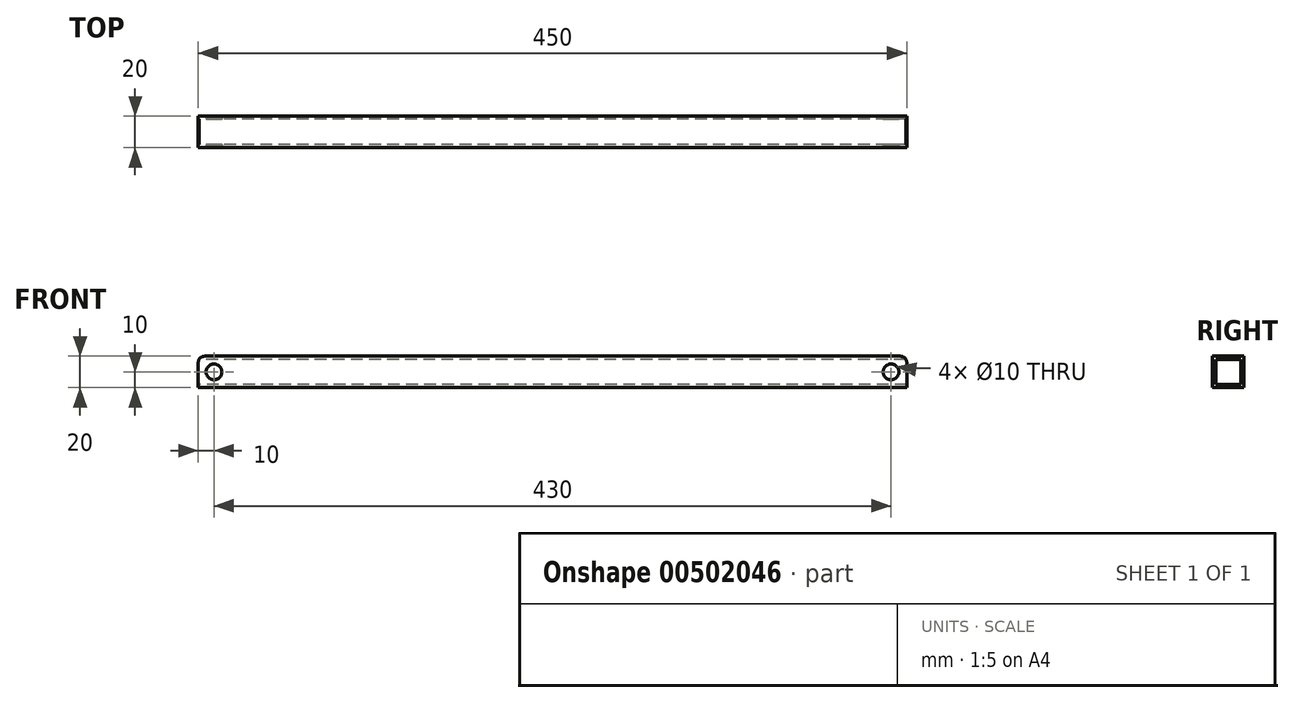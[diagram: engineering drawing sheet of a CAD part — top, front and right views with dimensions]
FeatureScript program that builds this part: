
annotation { "Feature Type Name" : "Feature", "Feature Type Description" : "" }
export const myFeature = defineFeature(function(context is Context, id is Id, definition is map)
    precondition{}
    {
        {
            var Q0;
            Q0=qCreatedBy(makeId("Right.planeOp"),FACE);
            var sketch = newSketch(context, id + "F0", { "sketchPlane" : qUnion([Q0])});
            skLineSegment(sketch, "E0.bottom", {"start": v(0, 0) * mm, "end": v(20, 0) * mm});
            skLineSegment(sketch, "E0.top", {"start": v(0, 20) * mm, "end": v(20, 20) * mm});
            skLineSegment(sketch, "E0.left", {"start": v(0, 0) * mm, "end": v(0, 20) * mm});
            skLineSegment(sketch, "E0.right", {"start": v(20, 0) * mm, "end": v(20, 20) * mm});
            skLineSegment(sketch, "E1.0", {"start": v(2, 18) * mm, "end": v(18, 18) * mm});
            skLineSegment(sketch, "E1.1", {"start": v(2, 2) * mm, "end": v(2, 18) * mm});
            skLineSegment(sketch, "E1.2", {"start": v(2, 2) * mm, "end": v(18, 2) * mm});
            skLineSegment(sketch, "E1.3", {"start": v(18, 2) * mm, "end": v(18, 18) * mm});
            skSolve(sketch);
        }
        {
            var Q0;
            Q0 = qSketchRegion(id + "F0", true);
            extrude(context, id + "F1", {"entities" : qUnion([Q0]), "depth" : 450 * mm});
        }
        {
            var Q0;
            Q0=makeQuery(id+"F1.opExtrude","SWEPT_FACE",FACE,{"disambiguationData":[OSD([sQuery(id+"F0.wireOp",EDGE,"E0.left")])]});
            var sketch = newSketch(context, id + "F2", { "sketchPlane" : qUnion([Q0])});
            skCircle(sketch, "E2", {"center": v(440, 10) * mm, "radius": 5 * mm});
            skSolve(sketch);
        }
        {
            var Q0;
            Q0 = qSketchRegion(id + "F2", true);
            extrude(context, id + "F3", {"entities" : qUnion([Q0]), "operationType" : NewBodyOperationType.REMOVE, "endBound" : BoundingType.THROUGH_ALL, "oppositeDirection" : true, "depth" : 25 * mm});
        }
        {
            var Q0;
            Q0=makeQuery(id+"F1.opExtrude","SWEPT_FACE",FACE,{"disambiguationData":[OSD([sQuery(id+"F0.wireOp",EDGE,"E0.left")])]});
            var sketch = newSketch(context, id + "F4", { "sketchPlane" : qUnion([Q0])});
            skCircle(sketch, "E3", {"center": v(10, 10) * mm, "radius": 5 * mm});
            skSolve(sketch);
        }
        {
            var Q0;
            Q0 = qSketchRegion(id + "F4", true);
            extrude(context, id + "F5", {"entities" : qUnion([Q0]), "operationType" : NewBodyOperationType.REMOVE, "endBound" : BoundingType.THROUGH_ALL, "oppositeDirection" : true, "depth" : 25 * mm});
        }
        {
            var Q0;
            Q0=makeQuery(id+"F1.opExtrude","CAP_EDGE",EDGE,{"disambiguationData":[OSD([sQuery(id+"F0.wireOp",EDGE,"E0.top")])],"isStart":false});
            fillet(context, id + "F6", {"entities" : qUnion([Q0]), "radius" : 4 * mm, "tangentPropagation" : true, "allowEdgeOverflow" : false});
        }
        {
            var Q0;
            Q0=makeQuery(id+"F1.opExtrude","CAP_EDGE",EDGE,{"disambiguationData":[OSD([sQuery(id+"F0.wireOp",EDGE,"E0.top")])],"isStart":true});
            fillet(context, id + "F7", {"entities" : qUnion([Q0]), "radius" : 4 * mm, "tangentPropagation" : true, "allowEdgeOverflow" : false});
        }
    });
